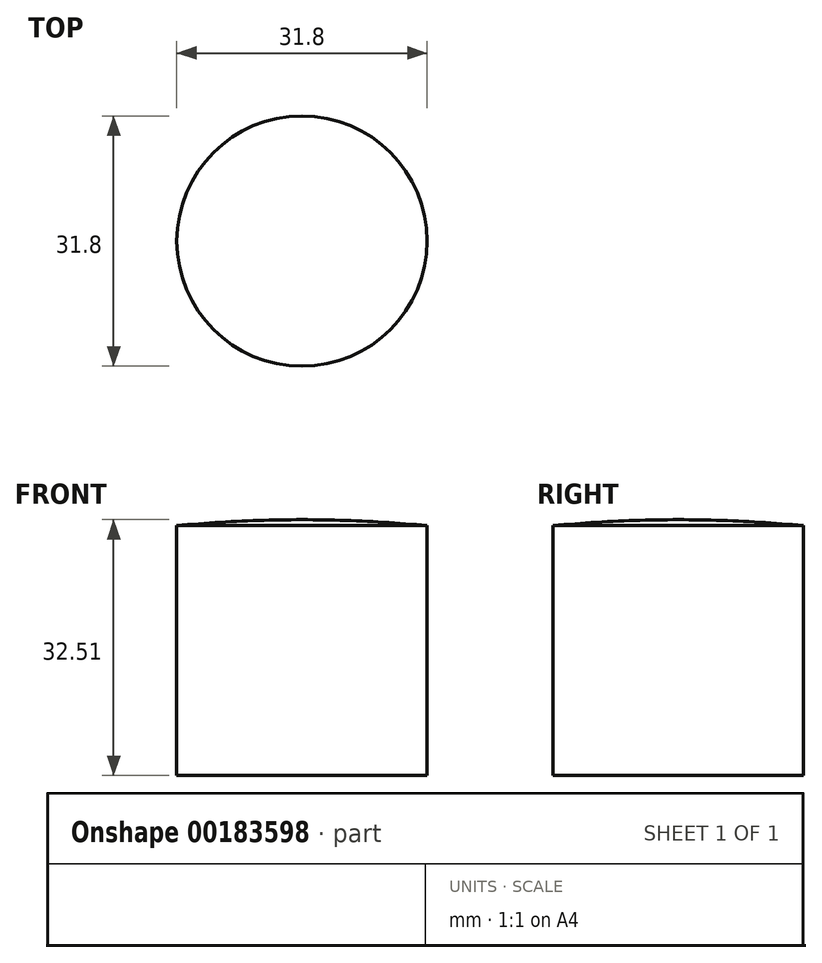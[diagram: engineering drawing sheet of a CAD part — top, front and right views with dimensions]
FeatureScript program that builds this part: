
annotation { "Feature Type Name" : "Feature", "Feature Type Description" : "" }
export const myFeature = defineFeature(function(context is Context, id is Id, definition is map)
    precondition{}
    {
        {
            var Q0;
            Q0=qCreatedBy(makeId("Front.planeOp"),FACE);
            var sketch = newSketch(context, id + "F0", { "sketchPlane" : qUnion([Q0])});
            skLineSegment(sketch, "E0", {"start": v(0, 132.97) * mm, "end": v(0, -164.72) * mm});
            skArc(sketch, "E1", {"start": v(0, -164.72) * mm, "mid": v(164.93, -7.58) * mm, "end": v(15.9, 164.72) * mm});
            skLineSegment(sketch, "E2", {"start": v(0, 132.97) * mm, "end": v(15.9, 132.97) * mm});
            skLineSegment(sketch, "E3", {"start": v(15.9, 132.97) * mm, "end": v(15.9, 164.72) * mm});
            skPoint(sketch, "E4.orphan", {"position": v(0, 165.48) * mm});
            skSolve(sketch);
        }
        {
            var Q0;
            Q0 = qSketchRegion(id + "F0", true);
            var Q1;
            Q1=sQuery(id+"F0.wireOp",EDGE,"E0");
            revolve(context, id + "F1", {"entities" : qUnion([Q0]), "axis" : qUnion([Q1]), "revolveType" : RevolveType.FULL});
        }
    });
